# Revit family: BNS1
name_source: partatom
category: Lighting Fixtures
units: mm (PartAtom-declared; Revit-internal decimal feet)

## family parameters
Always vertical = Yes
Cut with Voids When Loaded = No
Light Source = Yes
Part Type = Normal
Room Calculation Point = No
Round Connector Dimension = Use Diameter
Shared = No
Work Plane-Based = No

## types (1)
- BNS1
    Apparent Load = 0 VA
    Assembly Code = D5020200
    Color Filter = 16777215
    Default Elevation = 0"
    Description = Site/ Roadway Luminaire
    Dimming Lamp Color Temperature Shift = <None>
    Emit Shape Visible in Rendering = No
    Emit from Circle Diameter = 8"
    Finish = All colors shall be a Super TGIC thermoset polyester powder coat paint
    Full Load Current = 0 A
    Glass Material = Glass-Clear
    Housing Material = Metal-Aluminum Alloy
    Initial Lumens = 0 lm
    Inside Material = Metal-Aluminum-Reflective
    Lamp = LED
    Load Classification = Lighting
    Manufacturer = Kim Lighting
    MasterFormat Number = 26 56 16, 26 56 19, 26 56 29
    MasterFormat Title = Parking Lighting, Site Lighting, Walkway Lighting
    Model = BNS 1
    Note Text = LF
    Note Visible = Yes
    Number of Poles = 1
    OmniClass Number = 23-80 70 14 21
    OmniClass Title = Street and Roadway Lighting
    Photometric Notes = More IES files download on Photometric Web Link
    Photometric Web File = bns1h1e35-60l4k.ies
    Pole Material = Metal-Aluminum Alloy
    Pole Visible = Yes
    Power Factor = 1
    Series = Bounce
    Tilt Angle = 90.00°
    Total Pole Height = 192"
    Type Comments = Lighting Fixture
    URL = https://www.currentlighting.com
    Voltage = 120 V
    Wattage Comments = 60 LEDs, 66 W

## geometry (parser evidence)
native form markers: Blend x4, Sweep x6
no freeform markers — native parametric forms only
